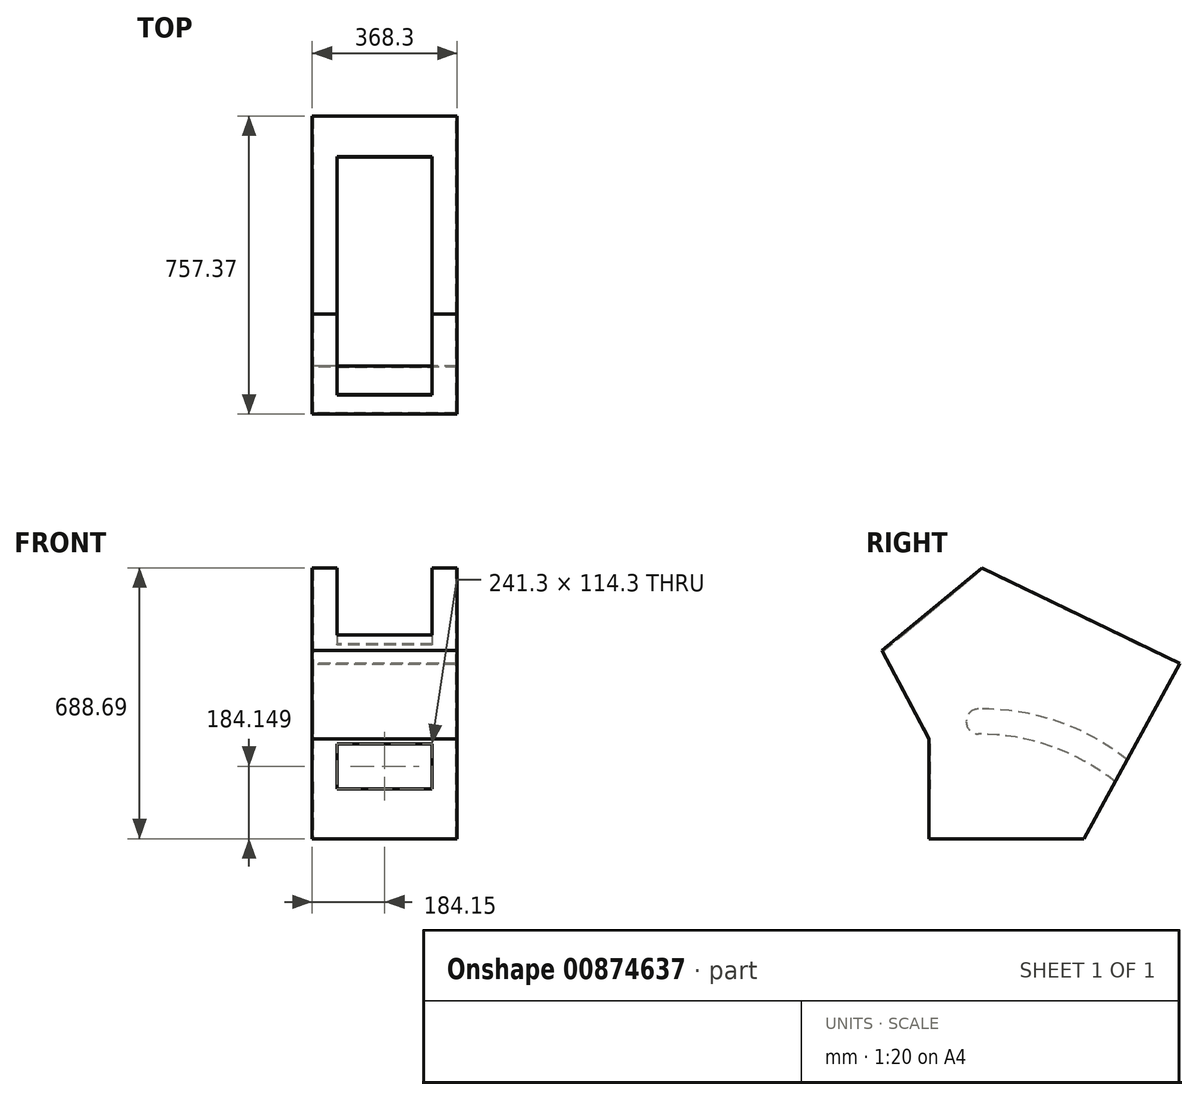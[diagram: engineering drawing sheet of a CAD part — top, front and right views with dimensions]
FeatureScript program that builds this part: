
annotation { "Feature Type Name" : "Feature", "Feature Type Description" : "" }
export const myFeature = defineFeature(function(context is Context, id is Id, definition is map)
    precondition{}
    {
        {
            var Q0;
            Q0=qCreatedBy(makeId("Right.planeOp"),FACE);
            var sketch = newSketch(context, id + "F0", { "sketchPlane" : qUnion([Q0])});
            skLineSegment(sketch, "E0", {"start": v(169.3, -219.58) * mm, "end": v(-224.4, -219.58) * mm});
            skLineSegment(sketch, "E1", {"start": v(-224.4, -219.58) * mm, "end": v(-224.4, 34.42) * mm});
            skLineSegment(sketch, "E2", {"start": v(-224.4, 34.42) * mm, "end": v(-344.27, 258.36) * mm});
            skLineSegment(sketch, "E3", {"start": v(-344.27, 258.36) * mm, "end": v(-90.08, 469.11) * mm});
            skLineSegment(sketch, "E4", {"start": v(-90.08, 469.11) * mm, "end": v(413.1, 226.09) * mm});
            skLineSegment(sketch, "E5", {"start": v(413.1, 226.09) * mm, "end": v(169.3, -219.58) * mm});
            skSolve(sketch);
        }
        {
            var Q0;
            Q0=qSketchRegion(id+"F0",true);
            extrude(context, id + "F1", {"entities" : qUnion([Q0]), "depth" : 368.3 * mm, "offsetDistance" : 25.4 * mm});
        }
        {
            var Q0;
            Q0=makeQuery(id+"F1.opExtrude","SWEPT_FACE",FACE,{"disambiguationData":[OSD([sQuery(id+"F0.wireOp",EDGE,"E5")])]});
            var Q1;
            Q1=makeQuery(id+"F1.opExtrude","SWEPT_FACE",FACE,{"disambiguationData":[OSD([sQuery(id+"F0.wireOp",EDGE,"E0")])]});
            shell(context, id + "F2", {"entities" : qUnion([Q0, Q1]), "thickness" : 2.54 * mm});
        }
        {
            var Q0;
            Q0=makeQuery(id+"F1.opExtrude","SWEPT_FACE",FACE,{"disambiguationData":[OSD([sQuery(id+"F0.wireOp",EDGE,"E4")])]});
            var sketch = newSketch(context, id + "F3", { "sketchPlane" : qUnion([Q0])});
            skLineSegment(sketch, "E6.bottom", {"start": v(304.8, -285.14) * mm, "end": v(63.5, -285.14) * mm});
            skLineSegment(sketch, "E6.top", {"start": v(304.8, 159.36) * mm, "end": v(63.5, 159.36) * mm});
            skLineSegment(sketch, "E6.left", {"start": v(304.8, -285.14) * mm, "end": v(304.8, 159.36) * mm});
            skLineSegment(sketch, "E6.right", {"start": v(63.5, -285.14) * mm, "end": v(63.5, 159.36) * mm});
            skSolve(sketch);
        }
        {
            var Q0;
            Q0=qSketchRegion(id+"F3",true);
            extrude(context, id + "F4", {"entities" : qUnion([Q0]), "operationType" : NewBodyOperationType.REMOVE, "oppositeDirection" : true, "depth" : 25.4 * mm, "offsetDistance" : 25.4 * mm});
        }
        {
            var Q0;
            Q0=makeQuery(id+"F1.opExtrude","SWEPT_FACE",FACE,{"disambiguationData":[OSD([sQuery(id+"F0.wireOp",EDGE,"E3")])]});
            var sketch = newSketch(context, id + "F5", { "sketchPlane" : qUnion([Q0])});
            skLineSegment(sketch, "E7.bottom", {"start": v(63.5, 230.07) * mm, "end": v(304.8, 230.07) * mm});
            skLineSegment(sketch, "E7.top", {"start": v(63.5, -36.63) * mm, "end": v(304.8, -36.63) * mm});
            skLineSegment(sketch, "E7.left", {"start": v(63.5, 230.07) * mm, "end": v(63.5, -36.63) * mm});
            skLineSegment(sketch, "E7.right", {"start": v(304.8, 230.07) * mm, "end": v(304.8, -36.63) * mm});
            skSolve(sketch);
        }
        {
            var Q0;
            Q0=qSketchRegion(id+"F5",true);
            extrude(context, id + "F6", {"entities" : qUnion([Q0]), "operationType" : NewBodyOperationType.REMOVE, "oppositeDirection" : true, "depth" : 25.4 * mm, "offsetDistance" : 25.4 * mm});
        }
        {
            var Q0;
            Q0=makeQuery(id+"F1.opExtrude","SWEPT_FACE",FACE,{"disambiguationData":[OSD([sQuery(id+"F0.wireOp",EDGE,"E1")])]});
            var sketch = newSketch(context, id + "F7", { "sketchPlane" : qUnion([Q0])});
            skLineSegment(sketch, "E8.bottom", {"start": v(63.5, 21.72) * mm, "end": v(304.8, 21.72) * mm});
            skLineSegment(sketch, "E8.top", {"start": v(63.5, -92.58) * mm, "end": v(304.8, -92.58) * mm});
            skLineSegment(sketch, "E8.left", {"start": v(63.5, 21.72) * mm, "end": v(63.5, -92.58) * mm});
            skLineSegment(sketch, "E8.right", {"start": v(304.8, 21.72) * mm, "end": v(304.8, -92.58) * mm});
            skSolve(sketch);
        }
        {
            var Q0;
            Q0=qSketchRegion(id+"F7",true);
            extrude(context, id + "F8", {"entities" : qUnion([Q0]), "operationType" : NewBodyOperationType.REMOVE, "oppositeDirection" : true, "depth" : 25.4 * mm, "offsetDistance" : 25.4 * mm});
        }
        {
            var Q0;
            {var subQ0=sQuery(id+"F0.wireOp",EDGE,"E5");var subQ1=sQuery(id+"F0.wireOp",EDGE,"E4");var subQ2=sQuery(id+"F0.wireOp",EDGE,"E3");var subQ3=sQuery(id+"F0.wireOp",EDGE,"E2");var subQ4=sQuery(id+"F0.wireOp",EDGE,"E1");var subQ5=sQuery(id+"F0.wireOp",EDGE,"E0");Q0=makeQuery(id+"F2.opShell","OFFSET_FACE",FACE,{"disambiguationData":[OSD([subQ5,subQ4,subQ3,subQ2,subQ1,subQ0]),TDD([makeQuery(id+"F1.opExtrude","CAP_FACE",FACE,{"disambiguationData":[OSD([subQ5,subQ4,subQ3,subQ2,subQ1,subQ0])],"isStart":true})])]});}
            var sketch = newSketch(context, id + "F9", { "sketchPlane" : qUnion([Q0])});
            skLineSegment(sketch, "E9", {"start": v(-224.4, 34.42) * mm, "end": v(-95.64, 34.42) * mm, "construction": true});
            skLineSegment(sketch, "E10", {"start": v(-95.64, 34.42) * mm, "end": v(58.05, 34.42) * mm, "construction": true});
            skLineSegment(sketch, "E11", {"start": v(-224.4, -219.58) * mm, "end": v(-98.61, -219.58) * mm});
            skLineSegment(sketch, "E12", {"start": v(-98.61, -219.58) * mm, "end": v(54.15, -219.58) * mm});
            skLineSegment(sketch, "E13", {"start": v(169.3, -219.58) * mm, "end": v(248.53, -74.74) * mm, "construction": true});
            skArc(sketch, "E14", {"start": v(248.53, -74.74) * mm, "mid": v(85.28, 15.47) * mm, "end": v(-98.61, 46.6) * mm});
            skArc(sketch, "E15", {"start": v(-98.61, 110.1) * mm, "mid": v(-130.36, 78.36) * mm, "end": v(-98.61, 46.6) * mm});
            skArc(sketch, "E16", {"start": v(279, -19.03) * mm, "mid": v(101.52, 78.63) * mm, "end": v(-98.61, 110.1) * mm});
            skSolve(sketch);
        }
        {
            var Q0;
            Q0=qSketchRegion(id+"F9",true);
            var Q1;
            {var subQ0=sQuery(id+"F9.wireOp",EDGE,"E14");Q1=makeQuery(id+"F9.imprint","IMPRINT",FACE,{"disambiguationData":[TD([[makeQuery(id+"F9.imprint","IMPRINT",EDGE,{"derivedFrom":subQ0}),-1.0]])]});}
            extrude(context, id + "F10", {"entities" : qUnion([Q0, Q1]), "operationType" : NewBodyOperationType.REMOVE, "oppositeDirection" : true, "depth" : 25.4 * mm, "offsetDistance" : 25.4 * mm});
        }
    });
